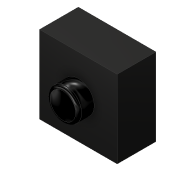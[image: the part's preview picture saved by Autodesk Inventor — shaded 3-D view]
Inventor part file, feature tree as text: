
AUTODESK INVENTOR PART (.ipt)
format: ipt  version: 2017 (Build 210142000, 142)  size: 116,736 bytes
history: native  units: in
note: dims shown in document units (in); Inventor stores cm internally (conversion verified against a paired STEP export)
features: extrude x2, sketch x2, fillet x1
ambient origin geometry x8: Origin, YZ Plane, XZ Plane, XY Plane, X Axis, Y Axis, Z Axis, Center Point
bodies: Solid1 (feature_tree)
feature tree (5):
  extrude  "Extrusion1"  Depth=0.512in
  extrude  "Extrusion2"  Depth=0.02in
  fillet  "Fillet1"  Radius=0.1024in
  sketch  "Sketch1"  dims[d0=0.512in d1=0.512in]
  sketch  "Sketch2"  dims[d2=0.2559in d3=0.0in d4=0.2087in d7=0.1024in d8=0.0in d9=0.02in]
